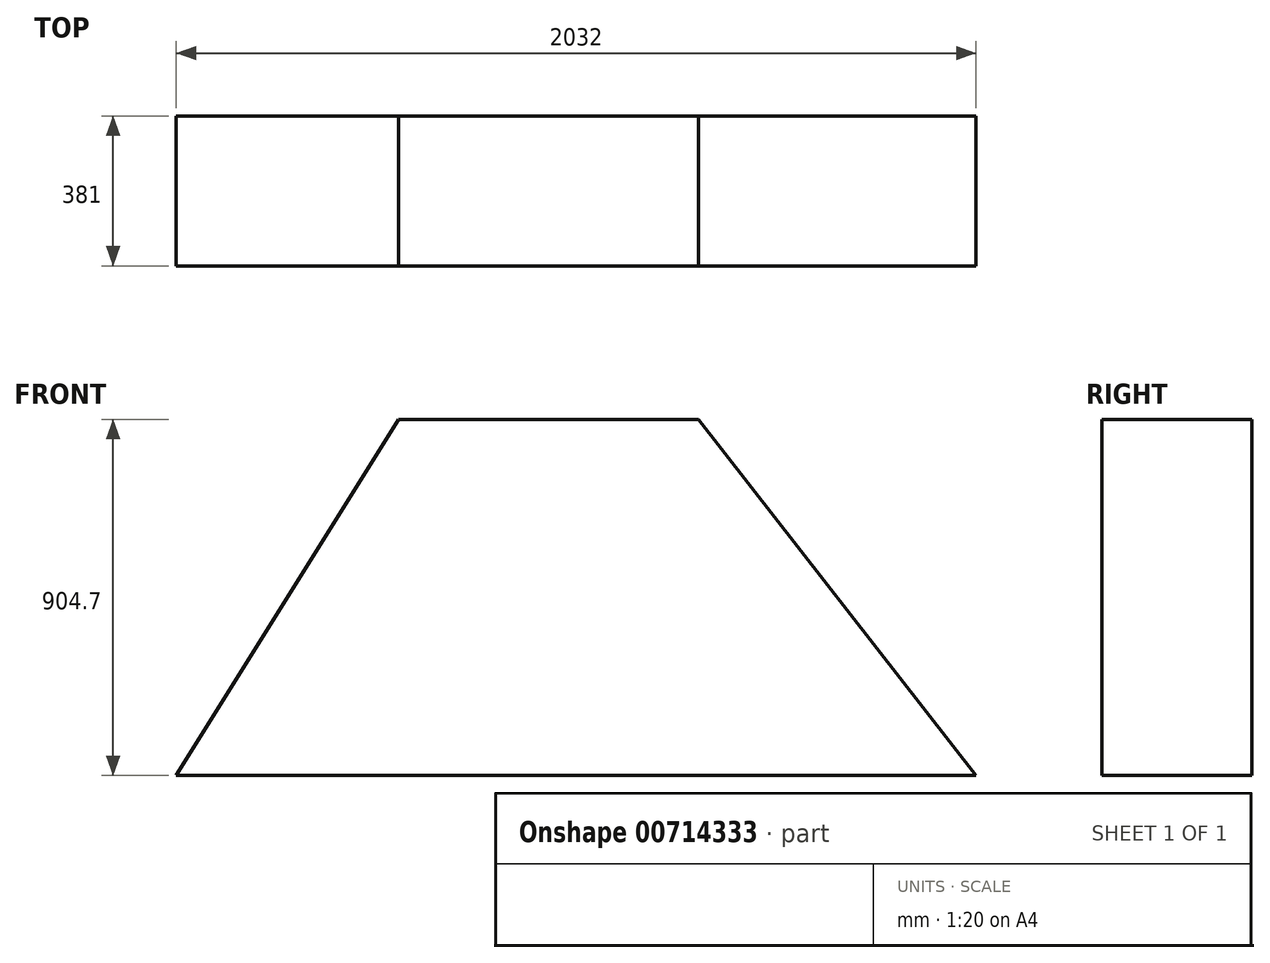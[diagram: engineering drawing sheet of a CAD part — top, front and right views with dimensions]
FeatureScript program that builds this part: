
annotation { "Feature Type Name" : "Feature", "Feature Type Description" : "" }
export const myFeature = defineFeature(function(context is Context, id is Id, definition is map)
    precondition{}
    {
        {
            var Q0;
            Q0=qCreatedBy(makeId("Front.planeOp"),FACE);
            var sketch = newSketch(context, id + "F0", { "sketchPlane" : qUnion([Q0])});
            skLineSegment(sketch, "E0", {"start": v(0, 0) * mm, "end": v(-565.32, -904.7) * mm});
            skLineSegment(sketch, "E1", {"start": v(-565.32, -904.7) * mm, "end": v(1466.68, -904.7) * mm});
            skLineSegment(sketch, "E2", {"start": v(0, 0) * mm, "end": v(762, 0) * mm});
            skLineSegment(sketch, "E3", {"start": v(762, 0) * mm, "end": v(1466.68, -904.7) * mm});
            skSolve(sketch);
        }
        {
            var Q0;
            Q0 = qSketchRegion(id + "F0", true);
            extrude(context, id + "F1", {"entities" : qUnion([Q0]), "depth" : 381 * mm, "offsetDistance" : 25.4 * mm});
        }
    });
